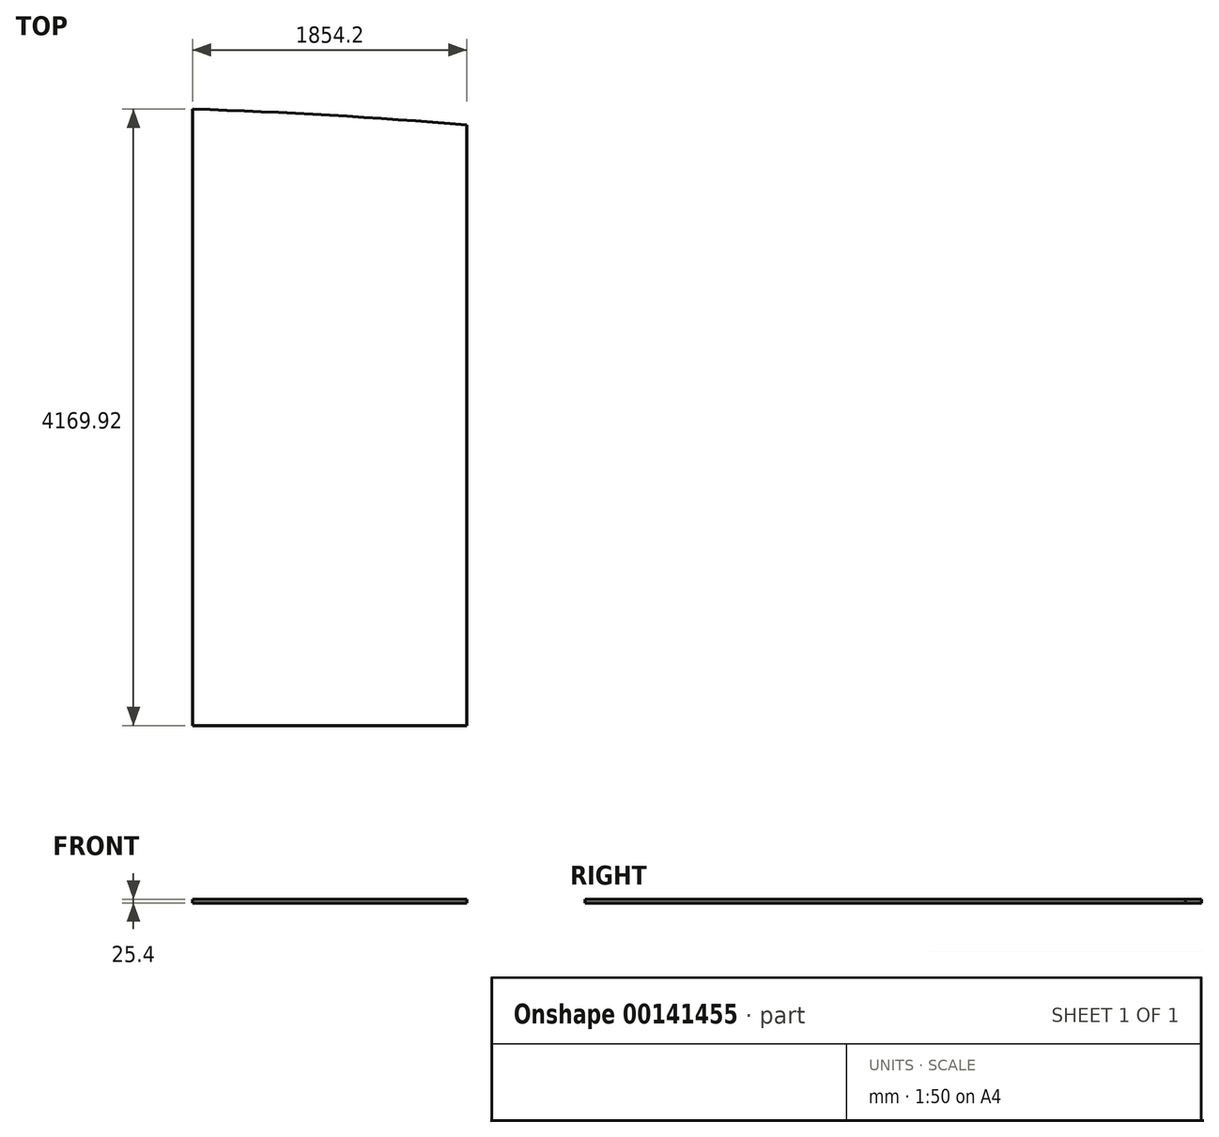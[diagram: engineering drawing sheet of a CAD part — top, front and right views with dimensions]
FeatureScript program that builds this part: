
annotation { "Feature Type Name" : "Feature", "Feature Type Description" : "" }
export const myFeature = defineFeature(function(context is Context, id is Id, definition is map)
    precondition{}
    {
        {
            var Q0;
            Q0=qCreatedBy(makeId("Top.planeOp"),FACE);
            var sketch = newSketch(context, id + "F0", { "sketchPlane" : qUnion([Q0])});
            skLineSegment(sketch, "E0", {"start": v(-730.98, 0) * mm, "end": v(1123.22, 0) * mm});
            skLineSegment(sketch, "E1", {"start": v(-730.98, 0) * mm, "end": v(-730.98, 4169.92) * mm});
            skLineSegment(sketch, "E2", {"start": v(1123.22, 0) * mm, "end": v(1123.22, 4061.46) * mm});
            skLineSegment(sketch, "E3", {"start": v(196.12, 0) * mm, "end": v(196.12, 4129.28) * mm});
            skArc(sketch, "E4", {"start": v(1123.22, 4061.46) * mm, "mid": v(196.9, 4129.23) * mm, "end": v(-730.98, 4169.92) * mm});
            skSolve(sketch);
        }
        {
            var Q0;
            {var subQ0=sQuery(id+"F0.wireOp",EDGE,"E1");Q0=makeQuery(id+"F0.imprint","IMPRINT",FACE,{"disambiguationData":[TD([[makeQuery(id+"F0.imprint","IMPRINT",EDGE,{"derivedFrom":subQ0}),-1.0]])]});}
            var Q1;
            {var subQ0=sQuery(id+"F0.wireOp",EDGE,"E2");Q1=makeQuery(id+"F0.imprint","IMPRINT",FACE,{"disambiguationData":[TD([[makeQuery(id+"F0.imprint","IMPRINT",EDGE,{"derivedFrom":subQ0}),1.0]])]});}
            extrude(context, id + "F1", {"entities" : qUnion([Q0, Q1]), "depth" : 25.4 * mm});
        }
    });
